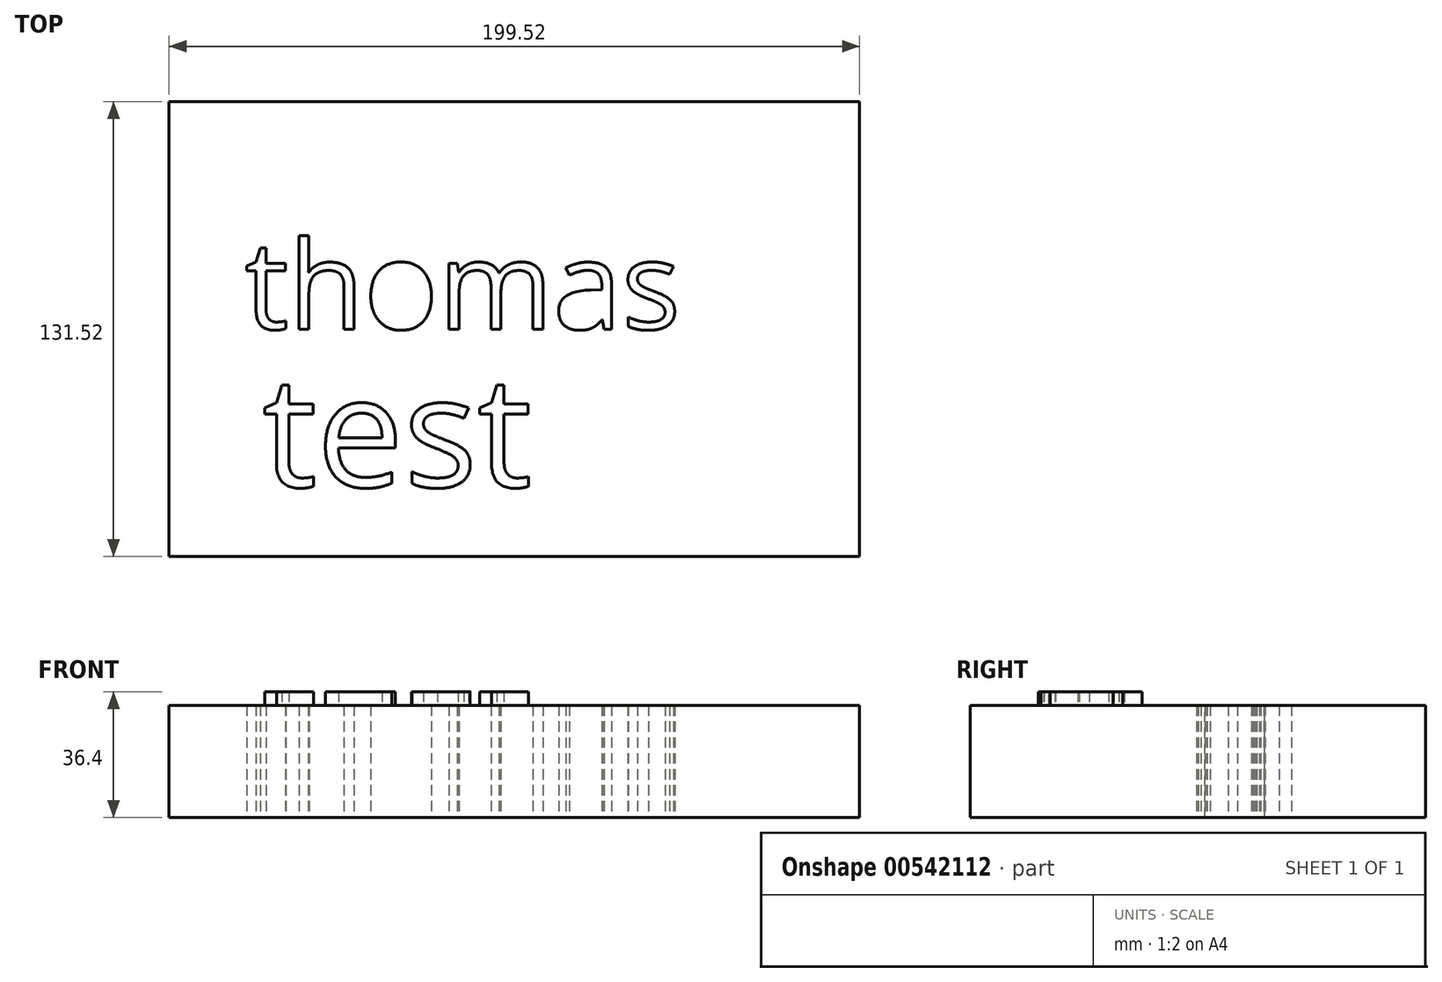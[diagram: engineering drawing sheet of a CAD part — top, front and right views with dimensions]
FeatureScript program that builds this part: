
annotation { "Feature Type Name" : "Feature", "Feature Type Description" : "" }
export const myFeature = defineFeature(function(context is Context, id is Id, definition is map)
    precondition{}
    {
        {
            var Q0;
            Q0=qCreatedBy(makeId("Top.planeOp"),FACE);
            var sketch = newSketch(context, id + "F0", { "sketchPlane" : qUnion([Q0])});
            skLineSegment(sketch, "E0.bottom", {"start": v(-99.76, 65.76) * mm, "end": v(99.76, 65.76) * mm});
            skLineSegment(sketch, "E0.top", {"start": v(-99.76, -65.76) * mm, "end": v(99.76, -65.76) * mm});
            skLineSegment(sketch, "E0.left", {"start": v(-99.76, 65.76) * mm, "end": v(-99.76, -65.76) * mm});
            skLineSegment(sketch, "E0.right", {"start": v(99.76, 65.76) * mm, "end": v(99.76, -65.76) * mm});
            skPoint(sketch, "E0.middle", {"position": v(0, 0) * mm});
            skText(sketch, "E1", { "text": "thomas\n", "fontName": "OpenSans-Regular.ttf"});
            const initialGuessF0  = {"E1": [-0.07787, 0, 1, 0, 0.02564]};
            skSetInitialGuess(sketch, initialGuessF0);
            skSolve(sketch);
        }
        {
            var Q0;
            Q0=makeQuery(id+"F0.imprint","IMPRINT",FACE,{"disambiguationData":[TD([[makeQuery(id+"F0.imprint","IMPRINT",EDGE,{"derivedFrom":sQuery(id+"F0.wireOp",EDGE,"E0.bottom")}),-1.0]])]});
            extrude(context, id + "F1", {"entities" : qUnion([Q0]), "depth" : 32.4 * mm, "offsetDistance" : 25 * mm});
        }
        {
            var Q0;
            Q0=makeQuery(id+"F1.opExtrude","CAP_FACE",FACE,{"disambiguationData":[OSD([sQuery(id+"F0.wireOp",EDGE,"E0.bottom"),sQuery(id+"F0.wireOp",EDGE,"E0.top"),sQuery(id+"F0.wireOp",EDGE,"E0.left"),sQuery(id+"F0.wireOp",EDGE,"E0.right"),sQuery(id+"F0.wireOp",EDGE,"E1.sketch_text.stroke-0"),sQuery(id+"F0.wireOp",EDGE,"E1.sketch_text.stroke-1"),sQuery(id+"F0.wireOp",EDGE,"E1.sketch_text.stroke-2"),sQuery(id+"F0.wireOp",EDGE,"E1.sketch_text.stroke-3"),sQuery(id+"F0.wireOp",EDGE,"E1.sketch_text.stroke-4"),sQuery(id+"F0.wireOp",EDGE,"E1.sketch_text.stroke-5"),sQuery(id+"F0.wireOp",EDGE,"E1.sketch_text.stroke-6"),sQuery(id+"F0.wireOp",EDGE,"E1.sketch_text.stroke-7"),sQuery(id+"F0.wireOp",EDGE,"E1.sketch_text.stroke-8"),sQuery(id+"F0.wireOp",EDGE,"E1.sketch_text.stroke-9"),sQuery(id+"F0.wireOp",EDGE,"E1.sketch_text.stroke-10"),sQuery(id+"F0.wireOp",EDGE,"E1.sketch_text.stroke-11"),sQuery(id+"F0.wireOp",EDGE,"E1.sketch_text.stroke-12"),sQuery(id+"F0.wireOp",EDGE,"E1.sketch_text.stroke-13"),sQuery(id+"F0.wireOp",EDGE,"E1.sketch_text.stroke-14"),sQuery(id+"F0.wireOp",EDGE,"E1.sketch_text.stroke-15"),sQuery(id+"F0.wireOp",EDGE,"E1.sketch_text.stroke-16"),sQuery(id+"F0.wireOp",EDGE,"E1.sketch_text.stroke-17"),sQuery(id+"F0.wireOp",EDGE,"E1.sketch_text.stroke-18"),sQuery(id+"F0.wireOp",EDGE,"E1.sketch_text.stroke-19"),sQuery(id+"F0.wireOp",EDGE,"E1.sketch_text.stroke-20"),sQuery(id+"F0.wireOp",EDGE,"E1.sketch_text.stroke-21"),sQuery(id+"F0.wireOp",EDGE,"E1.sketch_text.stroke-22"),sQuery(id+"F0.wireOp",EDGE,"E1.sketch_text.stroke-23"),sQuery(id+"F0.wireOp",EDGE,"E1.sketch_text.stroke-24"),sQuery(id+"F0.wireOp",EDGE,"E1.sketch_text.stroke-25"),sQuery(id+"F0.wireOp",EDGE,"E1.sketch_text.stroke-26"),sQuery(id+"F0.wireOp",EDGE,"E1.sketch_text.stroke-27"),sQuery(id+"F0.wireOp",EDGE,"E1.sketch_text.stroke-28"),sQuery(id+"F0.wireOp",EDGE,"E1.sketch_text.stroke-29"),sQuery(id+"F0.wireOp",EDGE,"E1.sketch_text.stroke-30"),sQuery(id+"F0.wireOp",EDGE,"E1.sketch_text.stroke-31"),sQuery(id+"F0.wireOp",EDGE,"E1.sketch_text.stroke-32"),sQuery(id+"F0.wireOp",EDGE,"E1.sketch_text.stroke-33"),sQuery(id+"F0.wireOp",EDGE,"E1.sketch_text.stroke-34"),sQuery(id+"F0.wireOp",EDGE,"E1.sketch_text.stroke-35"),sQuery(id+"F0.wireOp",EDGE,"E1.sketch_text.stroke-36"),sQuery(id+"F0.wireOp",EDGE,"E1.sketch_text.stroke-37"),sQuery(id+"F0.wireOp",EDGE,"E1.sketch_text.stroke-38"),sQuery(id+"F0.wireOp",EDGE,"E1.sketch_text.stroke-39"),sQuery(id+"F0.wireOp",EDGE,"E1.sketch_text.stroke-40"),sQuery(id+"F0.wireOp",EDGE,"E1.sketch_text.stroke-41"),sQuery(id+"F0.wireOp",EDGE,"E1.sketch_text.stroke-42"),sQuery(id+"F0.wireOp",EDGE,"E1.sketch_text.stroke-43"),sQuery(id+"F0.wireOp",EDGE,"E1.sketch_text.stroke-44"),sQuery(id+"F0.wireOp",EDGE,"E1.sketch_text.stroke-45"),sQuery(id+"F0.wireOp",EDGE,"E1.sketch_text.stroke-54"),sQuery(id+"F0.wireOp",EDGE,"E1.sketch_text.stroke-55"),sQuery(id+"F0.wireOp",EDGE,"E1.sketch_text.stroke-56"),sQuery(id+"F0.wireOp",EDGE,"E1.sketch_text.stroke-57"),sQuery(id+"F0.wireOp",EDGE,"E1.sketch_text.stroke-58"),sQuery(id+"F0.wireOp",EDGE,"E1.sketch_text.stroke-59"),sQuery(id+"F0.wireOp",EDGE,"E1.sketch_text.stroke-60"),sQuery(id+"F0.wireOp",EDGE,"E1.sketch_text.stroke-61"),sQuery(id+"F0.wireOp",EDGE,"E1.sketch_text.stroke-62"),sQuery(id+"F0.wireOp",EDGE,"E1.sketch_text.stroke-63"),sQuery(id+"F0.wireOp",EDGE,"E1.sketch_text.stroke-64"),sQuery(id+"F0.wireOp",EDGE,"E1.sketch_text.stroke-65"),sQuery(id+"F0.wireOp",EDGE,"E1.sketch_text.stroke-66"),sQuery(id+"F0.wireOp",EDGE,"E1.sketch_text.stroke-67"),sQuery(id+"F0.wireOp",EDGE,"E1.sketch_text.stroke-68"),sQuery(id+"F0.wireOp",EDGE,"E1.sketch_text.stroke-69"),sQuery(id+"F0.wireOp",EDGE,"E1.sketch_text.stroke-70"),sQuery(id+"F0.wireOp",EDGE,"E1.sketch_text.stroke-71"),sQuery(id+"F0.wireOp",EDGE,"E1.sketch_text.stroke-72"),sQuery(id+"F0.wireOp",EDGE,"E1.sketch_text.stroke-73"),sQuery(id+"F0.wireOp",EDGE,"E1.sketch_text.stroke-74"),sQuery(id+"F0.wireOp",EDGE,"E1.sketch_text.stroke-75"),sQuery(id+"F0.wireOp",EDGE,"E1.sketch_text.stroke-76"),sQuery(id+"F0.wireOp",EDGE,"E1.sketch_text.stroke-77"),sQuery(id+"F0.wireOp",EDGE,"E1.sketch_text.stroke-78"),sQuery(id+"F0.wireOp",EDGE,"E1.sketch_text.stroke-79"),sQuery(id+"F0.wireOp",EDGE,"E1.sketch_text.stroke-80"),sQuery(id+"F0.wireOp",EDGE,"E1.sketch_text.stroke-81"),sQuery(id+"F0.wireOp",EDGE,"E1.sketch_text.stroke-82"),sQuery(id+"F0.wireOp",EDGE,"E1.sketch_text.stroke-83"),sQuery(id+"F0.wireOp",EDGE,"E1.sketch_text.stroke-84"),sQuery(id+"F0.wireOp",EDGE,"E1.sketch_text.stroke-85"),sQuery(id+"F0.wireOp",EDGE,"E1.sketch_text.stroke-86"),sQuery(id+"F0.wireOp",EDGE,"E1.sketch_text.stroke-87"),sQuery(id+"F0.wireOp",EDGE,"E1.sketch_text.stroke-88"),sQuery(id+"F0.wireOp",EDGE,"E1.sketch_text.stroke-89"),sQuery(id+"F0.wireOp",EDGE,"E1.sketch_text.stroke-90"),sQuery(id+"F0.wireOp",EDGE,"E1.sketch_text.stroke-91"),sQuery(id+"F0.wireOp",EDGE,"E1.sketch_text.stroke-92"),sQuery(id+"F0.wireOp",EDGE,"E1.sketch_text.stroke-93"),sQuery(id+"F0.wireOp",EDGE,"E1.sketch_text.stroke-94"),sQuery(id+"F0.wireOp",EDGE,"E1.sketch_text.stroke-95"),sQuery(id+"F0.wireOp",EDGE,"E1.sketch_text.stroke-96"),sQuery(id+"F0.wireOp",EDGE,"E1.sketch_text.stroke-97"),sQuery(id+"F0.wireOp",EDGE,"E1.sketch_text.stroke-98"),sQuery(id+"F0.wireOp",EDGE,"E1.sketch_text.stroke-99"),sQuery(id+"F0.wireOp",EDGE,"E1.sketch_text.stroke-100"),sQuery(id+"F0.wireOp",EDGE,"E1.sketch_text.stroke-109"),sQuery(id+"F0.wireOp",EDGE,"E1.sketch_text.stroke-110"),sQuery(id+"F0.wireOp",EDGE,"E1.sketch_text.stroke-111"),sQuery(id+"F0.wireOp",EDGE,"E1.sketch_text.stroke-112"),sQuery(id+"F0.wireOp",EDGE,"E1.sketch_text.stroke-113"),sQuery(id+"F0.wireOp",EDGE,"E1.sketch_text.stroke-114"),sQuery(id+"F0.wireOp",EDGE,"E1.sketch_text.stroke-115"),sQuery(id+"F0.wireOp",EDGE,"E1.sketch_text.stroke-116"),sQuery(id+"F0.wireOp",EDGE,"E1.sketch_text.stroke-117"),sQuery(id+"F0.wireOp",EDGE,"E1.sketch_text.stroke-118"),sQuery(id+"F0.wireOp",EDGE,"E1.sketch_text.stroke-119"),sQuery(id+"F0.wireOp",EDGE,"E1.sketch_text.stroke-120"),sQuery(id+"F0.wireOp",EDGE,"E1.sketch_text.stroke-121"),sQuery(id+"F0.wireOp",EDGE,"E1.sketch_text.stroke-122"),sQuery(id+"F0.wireOp",EDGE,"E1.sketch_text.stroke-123"),sQuery(id+"F0.wireOp",EDGE,"E1.sketch_text.stroke-124"),sQuery(id+"F0.wireOp",EDGE,"E1.sketch_text.stroke-125"),sQuery(id+"F0.wireOp",EDGE,"E1.sketch_text.stroke-126"),sQuery(id+"F0.wireOp",EDGE,"E1.sketch_text.stroke-127"),sQuery(id+"F0.wireOp",EDGE,"E1.sketch_text.stroke-128"),sQuery(id+"F0.wireOp",EDGE,"E1.sketch_text.stroke-129"),sQuery(id+"F0.wireOp",EDGE,"E1.sketch_text.stroke-130"),sQuery(id+"F0.wireOp",EDGE,"E1.sketch_text.stroke-131"),sQuery(id+"F0.wireOp",EDGE,"E1.sketch_text.stroke-132"),sQuery(id+"F0.wireOp",EDGE,"E1.sketch_text.stroke-133")])],"isStart":false});
            var sketch = newSketch(context, id + "F2", { "sketchPlane" : qUnion([Q0])});
            skText(sketch, "E2", { "text": "test", "fontName": "OpenSans-Regular.ttf"});
            const initialGuessF2  = {"E2": [-0.07283, -0.0456, 1, 0, 0.03217]};
            skSetInitialGuess(sketch, initialGuessF2);
            skSolve(sketch);
        }
        {
            var Q0;
            Q0 = qSketchRegion(id + "F2", true);
            extrude(context, id + "F3", {"entities" : qUnion([Q0]), "operationType" : NewBodyOperationType.ADD, "depth" : 4 * mm, "offsetDistance" : 25 * mm});
        }
    });
